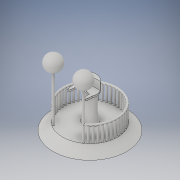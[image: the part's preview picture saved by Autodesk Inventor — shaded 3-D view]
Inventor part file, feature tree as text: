
AUTODESK INVENTOR PART (.ipt)
format: ipt  version: 2017 (Build 210142000, 142)  size: 735,744 bytes
history: native  units: in
note: dims shown in document units (in); Inventor stores cm internally (conversion verified against a paired STEP export)
features: other x20, sketch x9, extrude x6, loft x1, fillet x1
ambient origin geometry x7: Origin, YZ Plane, XY Plane, X Axis, Y Axis, Z Axis, Center Point
bodies: Body1 (feature_tree)
feature tree (37):
  other  "bace + terminal"
  other  "bace of terminal"
  other  "middle workplane"
  other  "middle"
  other  "top workplane"
  loft  "curved tower"
  extrude  "arm rests and terminal monitor"  Depth=0.8in
  other  "middle of the part vertical"
  other  "used to line up the key board and mouse"
  extrude  "bace"  Depth=1.8247in
  other  "ramp around"
  extrude  "railing bars"  Depth=1.0in
  other  "railing bar top workplane"
  other  "railing bar top"
  extrude  "light pole"  Depth=1.2in
  other  "globe light workplane"
  sketch  "Sketch20"  dims[d20=0.85in d27=1.1in]
  other  "light 1"
  other  "light 2"
  extrude  "line up slot"  Depth=1.1in
  other  "mate to back to monitor"
  extrude  "monitor raise"  Depth=1.0in
  fillet  "Fillet3"  Radius=0.65in
  other  "bottom workplane"
  other  "top"
  sketch  "Sketch15"  dims[d0=1.0in d1=0.75in]
  sketch  "Sketch16"  dims[d2=1.8247in d3=0.8in]
  sketch  "Sketch17"  dims[d4=0.55in d5=1.8247in]
  other  "Work Axis3"
  other  "Work Axis4"
  sketch  "Sketch18"  dims[d6=0.75in d7=1.0in]
  sketch  "Sketch19"  dims[d8=0.0in d9=90.0deg d10=0.0in d11=90.0deg d12=0.0in d13=90.0deg d19=1.2in]
  other  "Work Axis5"
  other  "Work Axis6"
  sketch  "Sketch21"  dims[d28=0.75in d29=1.0in d30=0.65in]
  sketch  "Sketch23"  dims[d42=1.1in d43=0.85in d44=1.0in d45=0.75in d49=1.2in d50=0.85in d51=1.0in d52=0.75in]
  sketch  "Sketch25"  dims[d122=7.0in d123=1.0in d124=0.0in d134=0.7579in d135=15.748in d137=1.9948in d139=2.0in d140=0.0in d141=0.2749in d142=90.0deg d143=0.25in d144=0.25in d145=90.0deg d146=4.0in d147=0.0in d150=2.0in d151=0.9in d152=2.0in d153=0.9in d155=90.0deg d156=90.0deg d157=0.0in d158=2.0in d159=0.2in d160=0.0in d163=0.8125in d165=0.4167in d166=0.8125in d167=0.4167in d168=0.2083in d169=0.0in d170=1.125in d173=1.8892in d174=1.1844in d175=1.125in d176=1.125in d177=1.1844in d178=1.0in d179=0.0in d180=0.5527in d181=0.01in]
